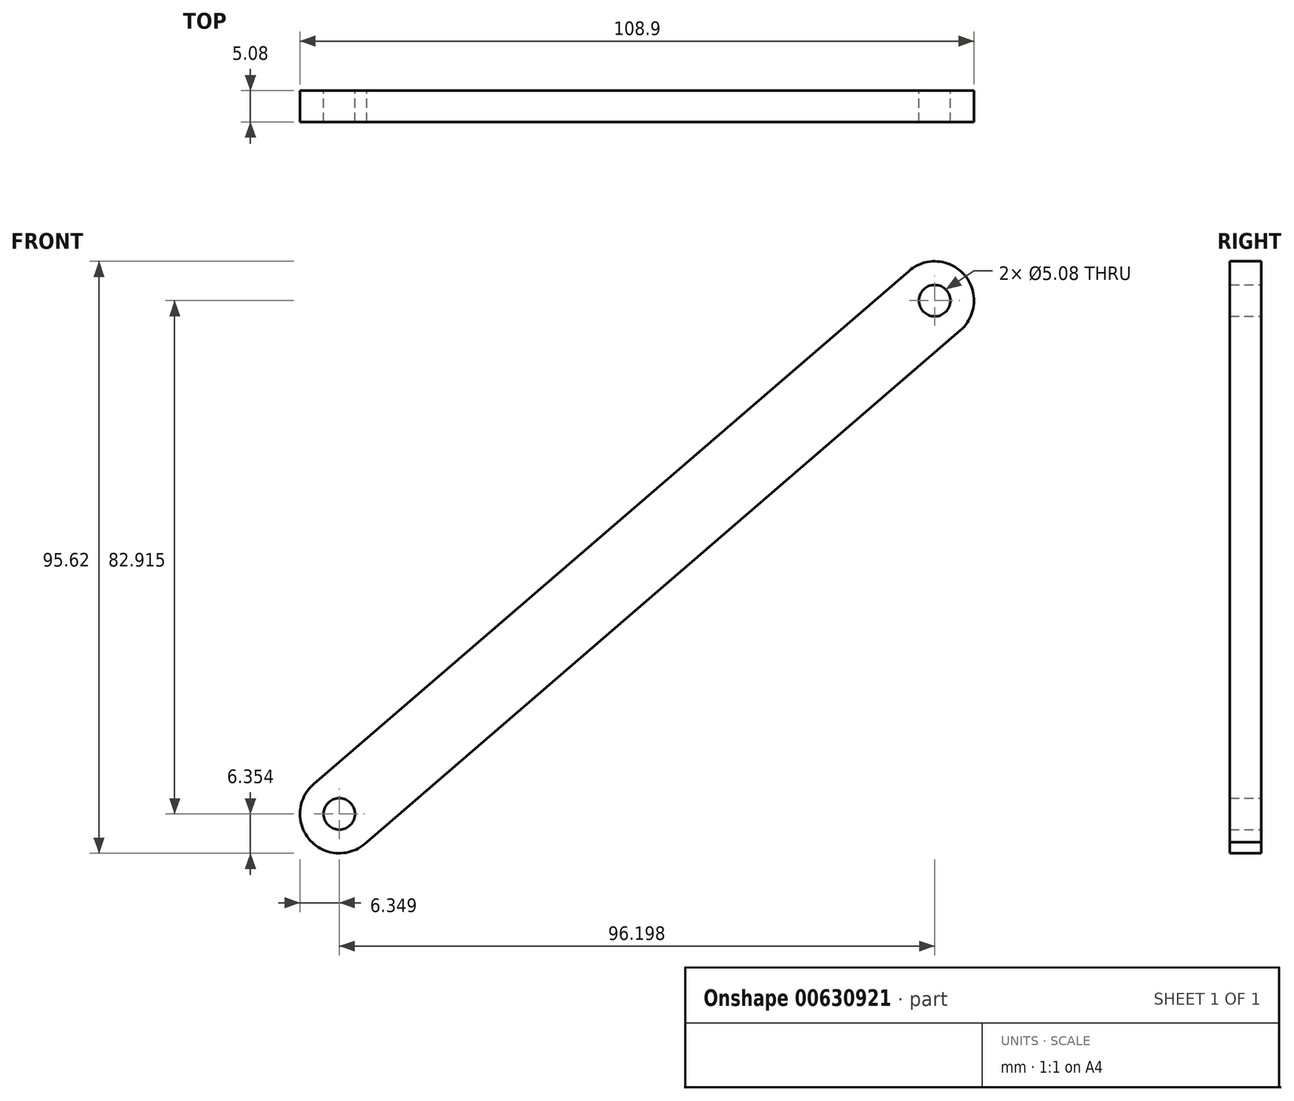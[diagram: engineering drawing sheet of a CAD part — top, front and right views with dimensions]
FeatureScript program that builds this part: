
annotation { "Feature Type Name" : "Feature", "Feature Type Description" : "" }
export const myFeature = defineFeature(function(context is Context, id is Id, definition is map)
    precondition{}
    {
        {
            var Q0;
            Q0=qCreatedBy(makeId("Front.planeOp"),FACE);
            var sketch = newSketch(context, id + "F0", { "sketchPlane" : qUnion([Q0])});
            skCircle(sketch, "E0", {"center": v(-53.35, -30.19) * mm, "radius": 6.35 * mm});
            skCircle(sketch, "E1", {"center": v(42.85, 52.73) * mm, "radius": 6.35 * mm});
            skCircle(sketch, "E2", {"center": v(42.85, 52.73) * mm, "radius": 2.54 * mm});
            skCircle(sketch, "E3", {"center": v(-53.35, -30.19) * mm, "radius": 2.54 * mm});
            skLineSegment(sketch, "E4", {"start": v(-57.5, -25.38) * mm, "end": v(38.7, 57.54) * mm});
            skLineSegment(sketch, "E5", {"start": v(-49.52, -35.25) * mm, "end": v(47, 47.92) * mm});
            skSolve(sketch);
        }
        {
            var Q0;
            Q0 = qSketchRegion(id + "F0", true);
            extrude(context, id + "F1", {"entities" : qUnion([Q0]), "depth" : 5.08 * mm, "offsetDistance" : 25.4 * mm});
        }
    });
